AUTODESK INVENTOR PART (.ipt)
format: ipt  version: 2021 (Build 250183000, 183)  size: 432,128 bytes
history: native  units: mm
features: extrude x16, other x12, fillet x5, sketch x1
ambient origin geometry x8: Origin, YZ Plane, XZ Plane, XY Plane, X Axis, Y Axis, Z Axis, Center Point
bodies: Body1 (feature_tree)
feature tree (34):
  extrude  "base"  Depth=95.0mm
  extrude  "walls"  Depth=2.6mm
  fillet  "inside"  Radius=58.0mm
  fillet  "outside"  Radius=24.5mm
  other  "cutout_usb_sketch"
  extrude  "cutout_usb"  Depth=58.0mm
  extrude  "cutout_usb_cover"  Depth=87.0mm
  extrude  "cutout_eth"  Depth=1.0mm
  fillet  "cutout_eth_and_usb_fillet"  Radius=2.0mm
  extrude  "cutout_stereo"  Depth=9.2mm TaperAngle=0.0deg
  fillet  "cutout_stereo_fillet"  Radius=3.0mm
  extrude  "cutout_button_rst"  Depth=7.0mm
  extrude  "cutout_audio"  Depth=1.0mm
  extrude  "cutout_usbc_pwr"  Depth=1.0mm
  extrude  "cutout_usbc_data"  Depth=1.0mm
  extrude  "cutout_hdmi"  Depth=1.0mm
  extrude  "cutout_gpio"  Depth=1.0mm
  extrude  "cutout_heatsink"  TaperAngle=0.0deg  [1 undecoded]
  fillet  "cutout_heatsink_gpio_fillet"  Radius=16.75mm
  extrude  "cutout_microusb"  Depth=23.94mm
  extrude  "cutout_fan_power"  TaperAngle=0.0deg  [1 undecoded]
  extrude  "Extrusion22"  Depth=10.0mm TaperAngle=0.0deg
  other  "cutout_eth_sketch"
  other  "cutout_stereo_sketch"
  other  "cutout_button_rst_sketch"
  other  "cutout_audio_sketch"
  other  "cutout_usbc_pwr_sketch"
  other  "cutout_usbc_data_sketch"
  other  "cutout_hdmi_sketch"
  other  "cutout_gpio_sketch"
  other  "cutout_heatsink_sketch"
  other  "cutout_microusb_sketch"
  other  "cutout_fan_power_sketch"
  sketch  "Sketch16"  dims[d0=66.0mm d1=95.0mm d14=2.6mm d15=20.0mm d17=58.0mm d18=20.0mm d20=49.0mm d24=24.5mm d25=58.0mm d26=87.0mm d27=4.5mm d51=2.0mm d52=0.0mm d53=9.2mm d54=0.0mm d57=3.0mm d58=7.0mm d66=4.5mm d68=4.5mm d76=7.4mm d77=14.8mm d78=17.02mm d81=0.0mm d82=0.0mm d84=16.75mm d85=23.94mm d86=0.0mm d87=0.0mm d88=10.0mm d89=0.0mm d90=11.92mm d91=11.56mm d93=5.27mm d94=0.0mm d95=0.0mm d96=9.0mm d97=9.102mm d98=10.192mm d99=3.0mm d100=0.0mm d101=0.0mm d102=4.0mm d103=2.225mm d104=2.225mm d106=7.2mm d109=10.0mm d110=0.0mm d111=20.366mm d112=3.55mm d113=31.83mm d114=12.74mm d115=10.0mm d116=0.0mm d117=5.43mm d118=2.0mm d119=46.73mm d120=12.74mm d121=5.43mm d122=2.0mm d123=10.0mm d124=0.0mm d125=13.35mm d126=19.0mm d127=10.0mm d128=0.0mm d129=5.525mm d130=2.0mm d131=2.0mm d132=7.0mm d133=2.6mm d134=2.6mm d135=10.0mm d136=0.0mm d137=10.0mm d138=0.0mm d147=0.5mm d148=2.0mm d149=0.5mm d150=0.5mm d151=68.394mm d152=11.499mm d153=2.0mm d154=0.0mm d155=0.0mm d156=5.75mm d157=2.0mm d165=12.05mm d166=9.0mm d168=40.0mm d169=2.0mm d170=0.0mm d171=2.0mm d172=33.7mm d173=8.0mm d175=33.6mm d176=0.0mm d177=1.0mm d178=2.0mm d179=0.0mm d180=1.0mm d181=11.92mm d183=0.0mm d184=2.0mm d185=0.0mm d186=0.0mm d187=6.5mm d188=1.0mm]
note: 2 required parameter values undecoded (feature->parameter linkage not recoverable at this tier; creation-order binding heuristic only, values carry confidence <= 0.55)
